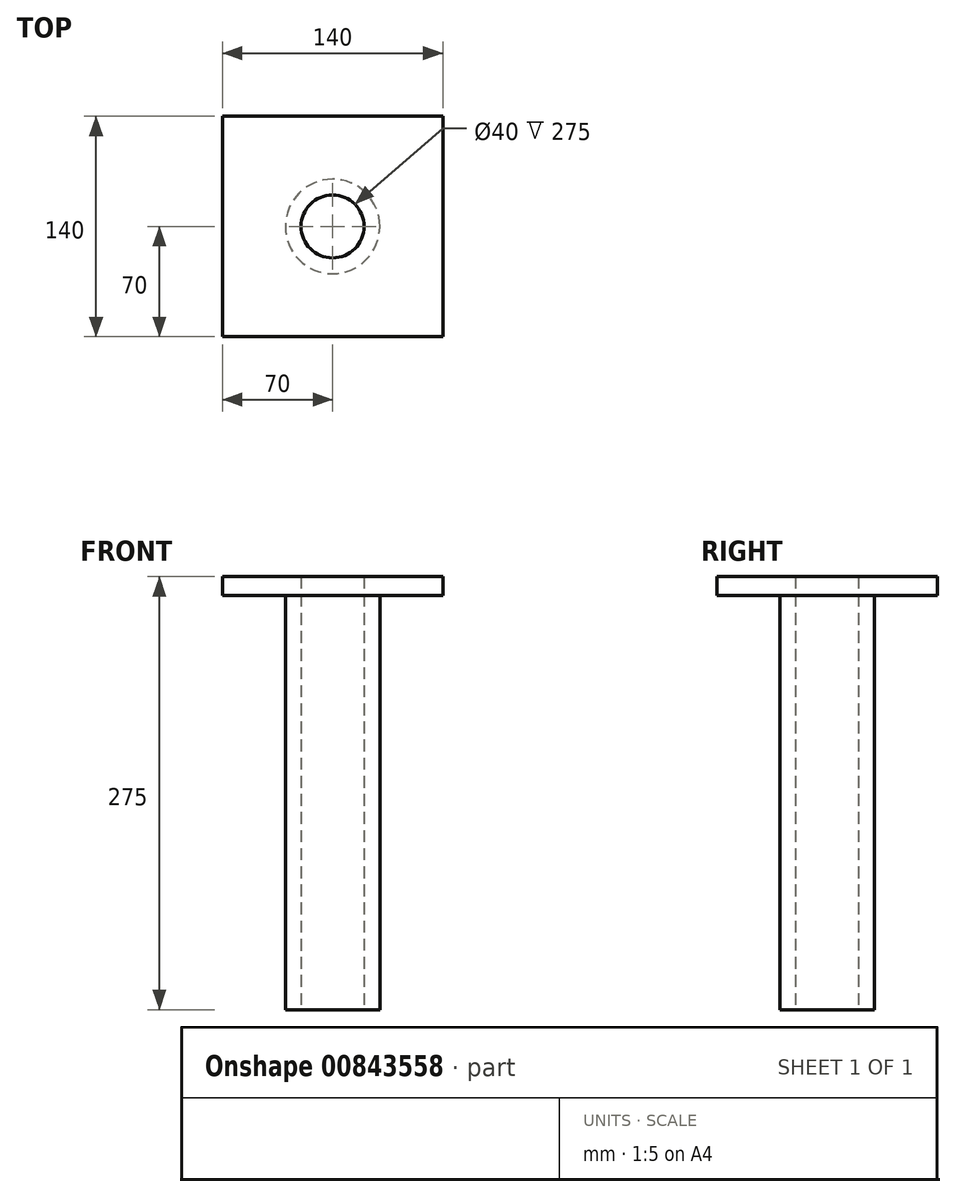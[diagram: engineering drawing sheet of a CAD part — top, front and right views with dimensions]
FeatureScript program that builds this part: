
annotation { "Feature Type Name" : "Feature", "Feature Type Description" : "" }
export const myFeature = defineFeature(function(context is Context, id is Id, definition is map)
    precondition{}
    {
        {
            var Q0;
            Q0=qCreatedBy(makeId("Top.planeOp"),FACE);
            var sketch = newSketch(context, id + "F0", { "sketchPlane" : qUnion([Q0])});
            skLineSegment(sketch, "E0.bottom", {"start": v(70, 70) * mm, "end": v(-70, 70) * mm});
            skLineSegment(sketch, "E0.top", {"start": v(70, -70) * mm, "end": v(-70, -70) * mm});
            skLineSegment(sketch, "E0.left", {"start": v(70, 70) * mm, "end": v(70, -70) * mm});
            skLineSegment(sketch, "E0.right", {"start": v(-70, 70) * mm, "end": v(-70, -70) * mm});
            skPoint(sketch, "E0.middle", {"position": v(0, 0) * mm});
            skSolve(sketch);
        }
        {
            var Q0;
            Q0 = qSketchRegion(id + "F0", true);
            extrude(context, id + "F1", {"entities" : qUnion([Q0]), "oppositeDirection" : true, "depth" : 12 * mm, "offsetDistance" : 25 * mm});
        }
        {
            var Q0;
            Q0=makeQuery(id+"F1.opExtrude","CAP_FACE",FACE,{"disambiguationData":[OSD([sQuery(id+"F0.wireOp",EDGE,"E0.bottom"),sQuery(id+"F0.wireOp",EDGE,"E0.top"),sQuery(id+"F0.wireOp",EDGE,"E0.left"),sQuery(id+"F0.wireOp",EDGE,"E0.right")])],"isStart":true});
            var sketch = newSketch(context, id + "F2", { "sketchPlane" : qUnion([Q0])});
            skCircle(sketch, "E1", {"center": v(0, 0) * mm, "radius": 30 * mm});
            skSolve(sketch);
        }
        {
            var Q0;
            Q0 = qSketchRegion(id + "F2", true);
            extrude(context, id + "F3", {"entities" : qUnion([Q0]), "operationType" : NewBodyOperationType.ADD, "oppositeDirection" : true, "depth" : 275 * mm, "offsetDistance" : 25 * mm});
        }
        {
            var Q0;
            Q0=makeQuery(id+"F3.opExtrude","CAP_FACE",FACE,{"disambiguationData":[OSD([sQuery(id+"F2.wireOp",EDGE,"E1")])],"isStart":false});
            var sketch = newSketch(context, id + "F4", { "sketchPlane" : qUnion([Q0])});
            skCircle(sketch, "E2", {"center": v(0, 0) * mm, "radius": 20 * mm});
            skSolve(sketch);
        }
        {
            var Q0;
            Q0 = qSketchRegion(id + "F4", true);
            extrude(context, id + "F5", {"entities" : qUnion([Q0]), "operationType" : NewBodyOperationType.REMOVE, "endBound" : BoundingType.THROUGH_ALL, "oppositeDirection" : true, "depth" : 25 * mm, "offsetDistance" : 25 * mm});
        }
    });
